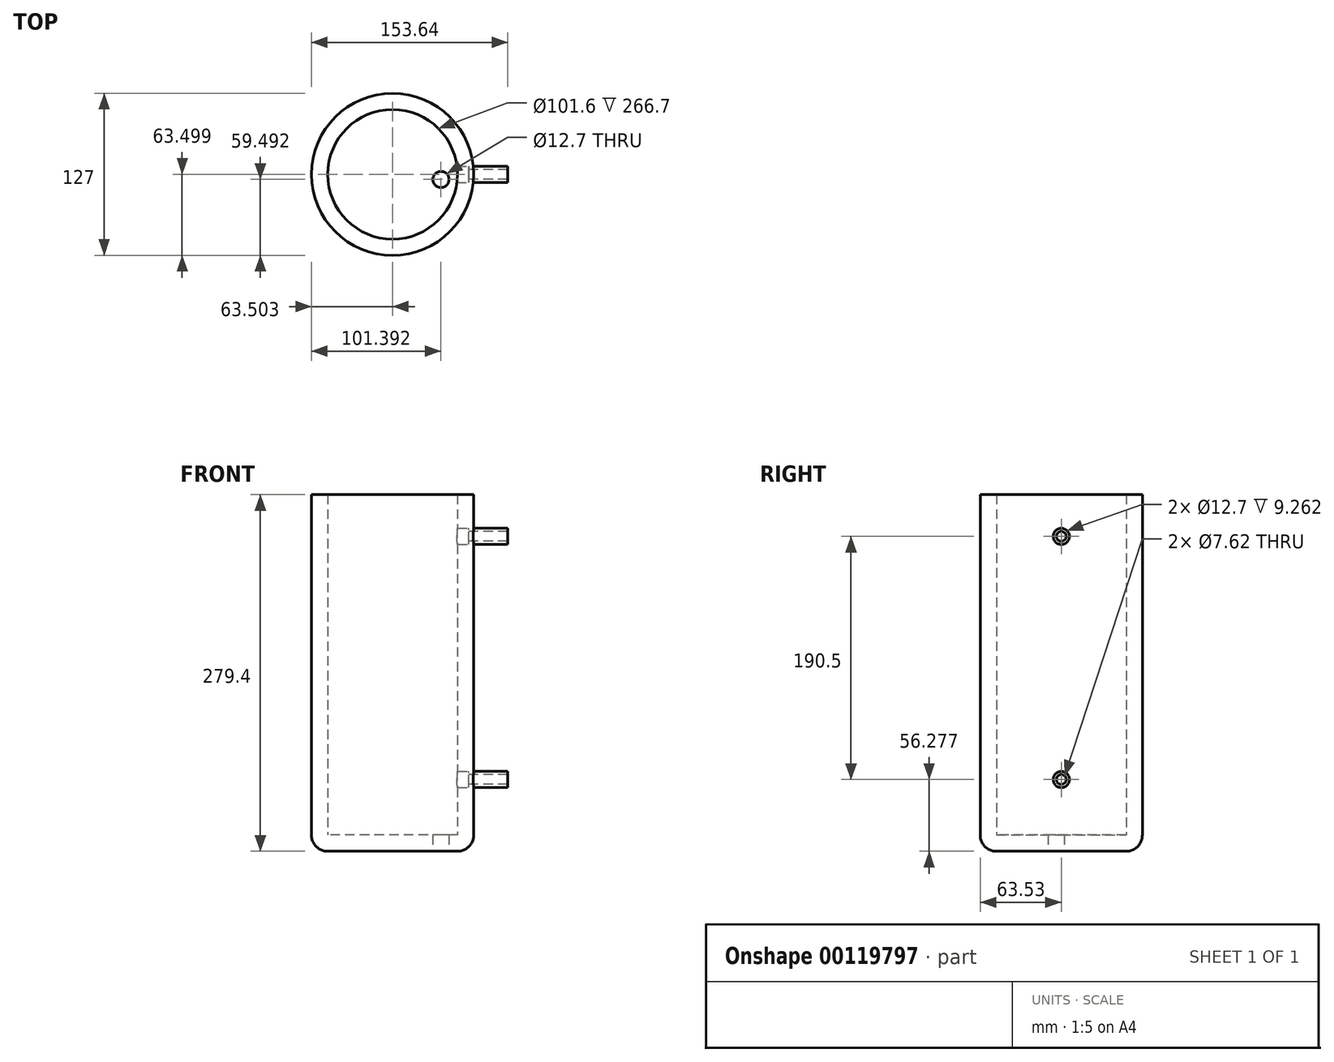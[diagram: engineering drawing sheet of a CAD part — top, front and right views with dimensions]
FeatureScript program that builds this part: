
annotation { "Feature Type Name" : "Feature", "Feature Type Description" : "" }
export const myFeature = defineFeature(function(context is Context, id is Id, definition is map)
    precondition{}
    {
        {
            var Q0;
            Q0=qCreatedBy(makeId("Top.planeOp"),FACE);
            var sketch = newSketch(context, id + "F0", { "sketchPlane" : qUnion([Q0])});
            skCircle(sketch, "E0", {"center": v(-64.74, 44.42) * mm, "radius": 63.5 * mm});
            skSolve(sketch);
        }
        {
            var Q0;
            Q0 = qSketchRegion(id + "F0", true);
            extrude(context, id + "F1", {"entities" : qUnion([Q0]), "depth" : 279.4 * mm});
        }
        {
            var Q0;
            Q0=makeQuery(id+"F1.opExtrude","CAP_FACE",FACE,{"disambiguationData":[OSD([sQuery(id+"F0.wireOp",EDGE,"E0")])],"isStart":false});
            shell(context, id + "F2", {"entities" : qUnion([Q0]), "thickness" : 12.7 * mm});
        }
        {
            var Q0;
            Q0=makeQuery(id+"F1.opExtrude","CAP_FACE",FACE,{"disambiguationData":[OSD([sQuery(id+"F0.wireOp",EDGE,"E0")])],"isStart":true});
            var sketch = newSketch(context, id + "F3", { "sketchPlane" : qUnion([Q0])});
            skCircle(sketch, "E1", {"center": v(-26.85, -40.41) * mm, "radius": 6.35 * mm});
            skSolve(sketch);
        }
        {
            var Q0;
            Q0 = qSketchRegion(id + "F3", true);
            extrude(context, id + "F4", {"entities" : qUnion([Q0]), "operationType" : NewBodyOperationType.REMOVE, "endBound" : BoundingType.THROUGH_ALL, "oppositeDirection" : true, "depth" : 25.4 * mm});
        }
        {
            var Q0;
            Q0=qCreatedBy(makeId("Right.planeOp"),FACE);
            var sketch = newSketch(context, id + "F5", { "sketchPlane" : qUnion([Q0])});
            skCircle(sketch, "E2", {"center": v(44.45, 56.28) * mm, "radius": 6.35 * mm});
            skCircle(sketch, "E3", {"center": v(44.45, 246.78) * mm, "radius": 6.35 * mm});
            skLineSegment(sketch, "E4", {"start": v(44.45, 56.28) * mm, "end": v(44.45, 246.78) * mm});
            skSolve(sketch);
        }
        {
            var Q0;
            Q0 = qSketchRegion(id + "F5", true);
            extrude(context, id + "F6", {"entities" : qUnion([Q0]), "operationType" : NewBodyOperationType.REMOVE, "oppositeDirection" : true, "depth" : 50.8 * mm});
        }
        {
            var Q0;
            Q0=qCreatedBy(makeId("Right.planeOp"),FACE);
            var sketch = newSketch(context, id + "F7", { "sketchPlane" : qUnion([Q0])});
            skCircle(sketch, "E5", {"center": v(44.45, 246.78) * mm, "radius": 3.81 * mm});
            skCircle(sketch, "E6", {"center": v(44.45, 56.28) * mm, "radius": 3.81 * mm});
            skCircle(sketch, "E7", {"center": v(44.45, 246.78) * mm, "radius": 6.35 * mm});
            skCircle(sketch, "E8", {"center": v(44.45, 56.28) * mm, "radius": 6.35 * mm});
            skSolve(sketch);
        }
        {
            var Q0;
            Q0=makeQuery(id+"F7.imprint","IMPRINT",FACE,{"disambiguationData":[TD([[makeQuery(id+"F7.imprint","IMPRINT",EDGE,{"derivedFrom":sQuery(id+"F7.wireOp",EDGE,"E5")}),-1.0]])]});
            var Q1;
            Q1=makeQuery(id+"F7.imprint","IMPRINT",FACE,{"disambiguationData":[TD([[makeQuery(id+"F7.imprint","IMPRINT",EDGE,{"derivedFrom":sQuery(id+"F7.wireOp",EDGE,"E6")}),-1.0]])]});
            extrude(context, id + "F8", {"entities" : qUnion([Q0, Q1]), "operationType" : NewBodyOperationType.ADD, "depth" : 25.4 * mm, "hasSecondDirection" : true, "secondDirectionOppositeDirection" : true, "secondDirectionDepth" : 5.08 * mm});
        }
        {
            var Q0;
            Q0=makeQuery(id+"F1.opExtrude","CAP_EDGE",EDGE,{"disambiguationData":[OSD([sQuery(id+"F0.wireOp",EDGE,"E0")])],"isStart":true});
            fillet(context, id + "F9", {"entities" : qUnion([Q0]), "radius" : 12.7 * mm, "tangentPropagation" : true, "allowEdgeOverflow" : false});
        }
    });
